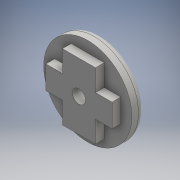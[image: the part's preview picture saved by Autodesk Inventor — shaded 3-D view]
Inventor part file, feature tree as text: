
AUTODESK INVENTOR PART (.ipt)
format: ipt  version: 2016 (Build 200138000, 138)  size: 151,040 bytes
history: native  units: mm
features: other x4, extrude x2, hole x2, fillet x1
ambient origin geometry x8: Origin, YZ Plane, XZ Plane, XY Plane, X Axis, Y Axis, Z Axis, Center Point
bodies: Body1 (feature_tree)
feature tree (9):
  other  "zero_sketch.ipt"
  extrude  "Extrusion1"  Depth=10.0mm
  extrude  "Extrusion2"  Depth=0.6mm TaperAngle=0.0deg
  hole  "Hole1"  [1 undecoded]
  hole  "Hole2"  [1 undecoded]
  fillet  "Fillet1"  Radius=10.0mm
  other  "base+body"
  other  "base+body_1"
  other  "base+body_2"
note: 2 required parameter values undecoded (feature->parameter linkage not recoverable at this tier; creation-order binding heuristic only, values carry confidence <= 0.55)
